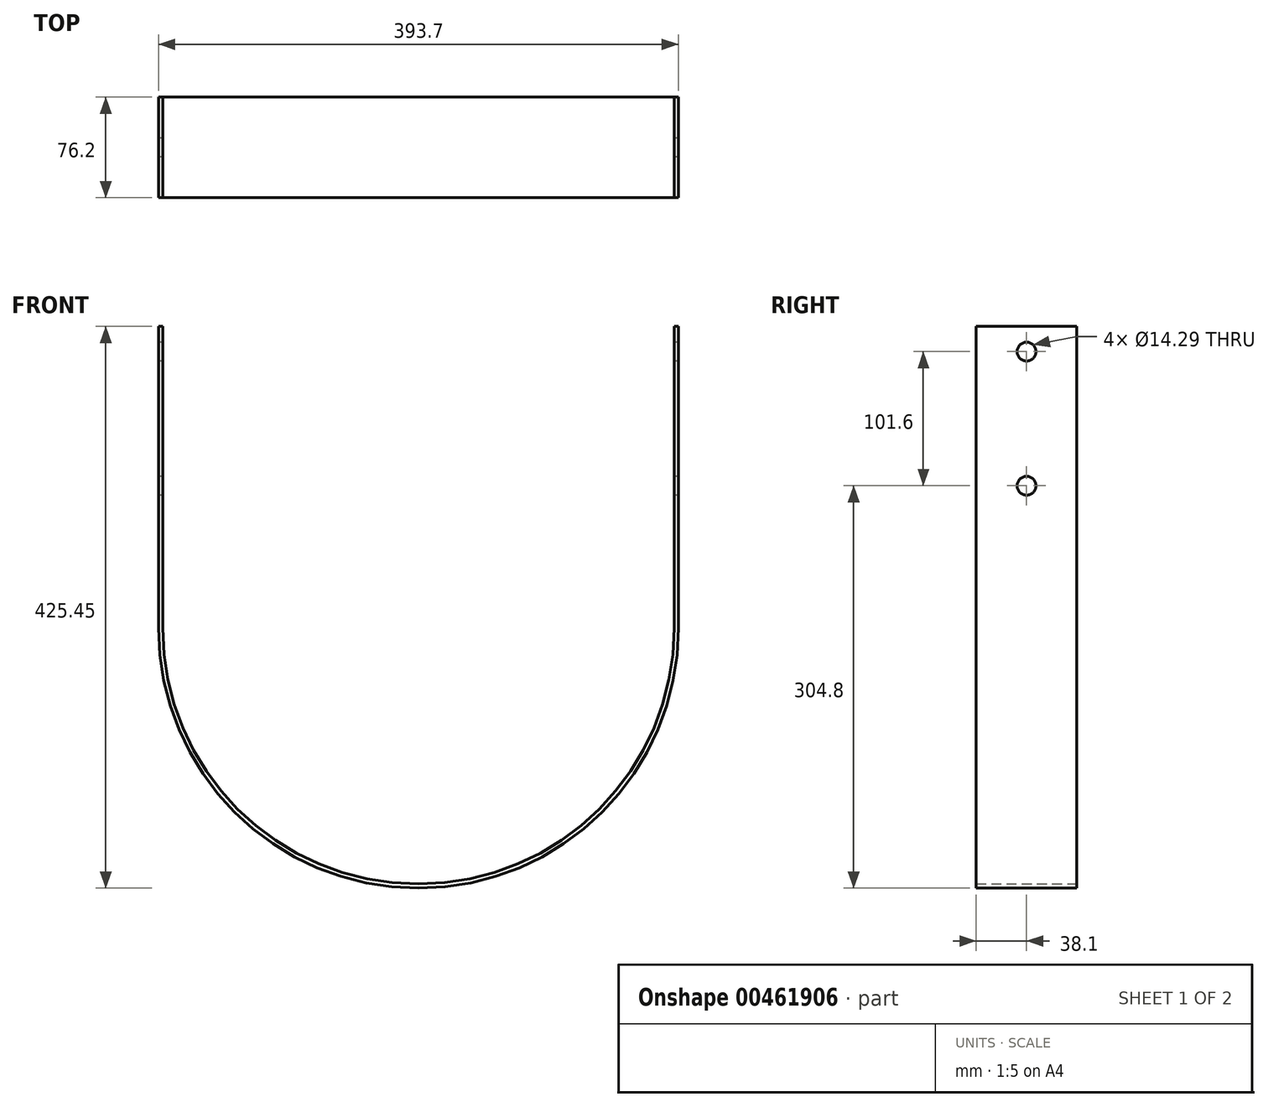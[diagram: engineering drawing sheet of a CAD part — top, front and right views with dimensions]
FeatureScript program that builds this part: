
annotation { "Feature Type Name" : "Feature", "Feature Type Description" : "" }
export const myFeature = defineFeature(function(context is Context, id is Id, definition is map)
    precondition{}
    {
        {
            var Q0;
            Q0=qCreatedBy(makeId("Front.planeOp"),FACE);
            var sketch = newSketch(context, id + "F0", { "sketchPlane" : qUnion([Q0])});
            skArc(sketch, "E0", {"start": v(-193.68, 0) * mm, "mid": v(0, -193.68) * mm, "end": v(193.68, 0) * mm});
            skArc(sketch, "E1", {"start": v(-196.85, 0) * mm, "mid": v(0, -196.85) * mm, "end": v(196.85, 0) * mm});
            skLineSegment(sketch, "E2", {"start": v(-193.68, 0) * mm, "end": v(-193.68, 228.6) * mm});
            skLineSegment(sketch, "E3", {"start": v(-193.68, 228.6) * mm, "end": v(-196.85, 228.6) * mm});
            skLineSegment(sketch, "E4", {"start": v(-196.85, 228.6) * mm, "end": v(-196.85, 0) * mm});
            skLineSegment(sketch, "E5", {"start": v(196.85, 0) * mm, "end": v(196.85, 228.6) * mm});
            skLineSegment(sketch, "E6", {"start": v(196.85, 228.6) * mm, "end": v(193.68, 228.6) * mm});
            skLineSegment(sketch, "E7", {"start": v(193.68, 228.6) * mm, "end": v(193.68, 0) * mm});
            skSolve(sketch);
        }
        {
            var Q0;
            Q0 = qSketchRegion(id + "F0", true);
            extrude(context, id + "F1", {"entities" : qUnion([Q0]), "endBound" : BoundingType.SYMMETRIC, "depth" : 76.2 * mm});
        }
        {
            var Q0;
            Q0=makeQuery(id+"F1.opExtrude","SWEPT_FACE",FACE,{"disambiguationData":[OSD([sQuery(id+"F0.wireOp",EDGE,"E4")])]});
            var sketch = newSketch(context, id + "F2", { "sketchPlane" : qUnion([Q0])});
            skCircle(sketch, "E8", {"center": v(0, 209.55) * mm, "radius": 7.14 * mm});
            skPoint(sketch, "E8.centerSnap0", {"position": v(0, 228.6) * mm});
            skCircle(sketch, "E9", {"center": v(0, 107.95) * mm, "radius": 7.14 * mm});
            skSolve(sketch);
        }
        {
            var Q0;
            Q0 = qSketchRegion(id + "F2", true);
            extrude(context, id + "F3", {"entities" : qUnion([Q0]), "operationType" : NewBodyOperationType.REMOVE, "oppositeDirection" : true, "depth" : 508 * mm});
        }
    });
